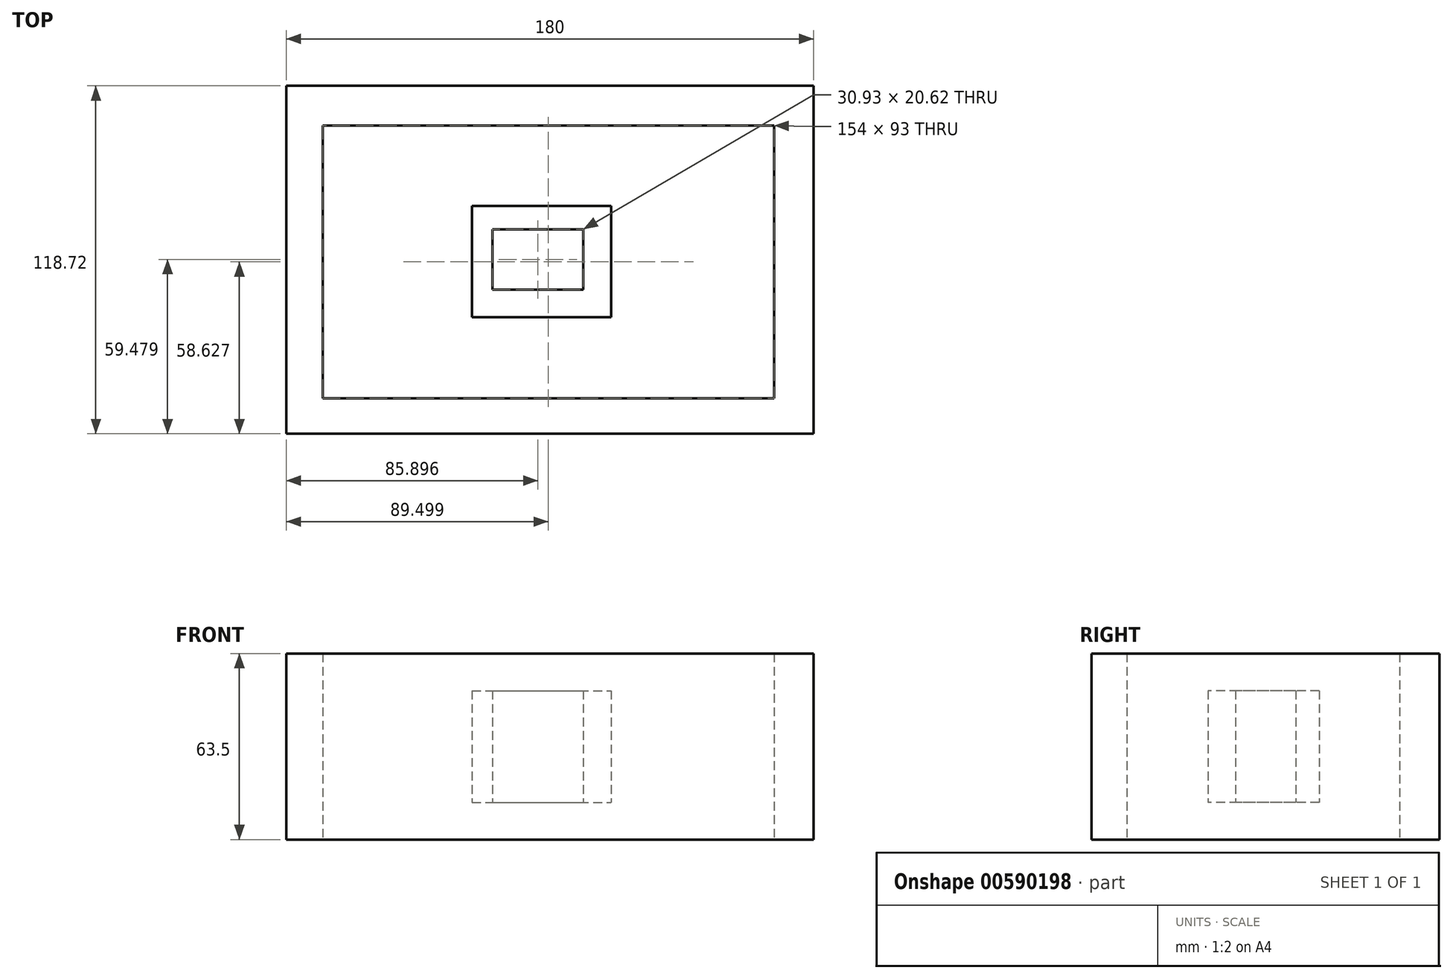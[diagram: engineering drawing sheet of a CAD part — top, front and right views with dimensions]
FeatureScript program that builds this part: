
annotation { "Feature Type Name" : "Feature", "Feature Type Description" : "" }
export const myFeature = defineFeature(function(context is Context, id is Id, definition is map)
    precondition{}
    {
        {
            var Q0;
            Q0=qCreatedBy(makeId("Top.planeOp"),FACE);
            var sketch = newSketch(context, id + "F0", { "sketchPlane" : qUnion([Q0])});
            skLineSegment(sketch, "E0.bottom", {"start": v(-86, 59.95) * mm, "end": v(94, 59.95) * mm});
            skLineSegment(sketch, "E0.top", {"start": v(-86, -58.77) * mm, "end": v(94, -58.77) * mm});
            skLineSegment(sketch, "E0.left", {"start": v(-86, 59.95) * mm, "end": v(-86, -58.77) * mm});
            skLineSegment(sketch, "E0.right", {"start": v(94, 59.95) * mm, "end": v(94, -58.77) * mm});
            skLineSegment(sketch, "E1.bottom", {"start": v(-22.6, 18.99) * mm, "end": v(24.97, 18.99) * mm});
            skLineSegment(sketch, "E1.top", {"start": v(-22.6, -18.99) * mm, "end": v(24.97, -18.99) * mm});
            skLineSegment(sketch, "E1.left", {"start": v(-22.6, 18.99) * mm, "end": v(-22.6, -18.99) * mm});
            skLineSegment(sketch, "E1.right", {"start": v(24.97, 18.99) * mm, "end": v(24.97, -18.99) * mm});
            skLineSegment(sketch, "E2.bottom", {"start": v(-73.5, 46.36) * mm, "end": v(80.5, 46.36) * mm});
            skLineSegment(sketch, "E2.top", {"start": v(-73.5, -46.64) * mm, "end": v(80.5, -46.64) * mm});
            skLineSegment(sketch, "E2.left", {"start": v(-73.5, 46.36) * mm, "end": v(-73.5, -46.64) * mm});
            skLineSegment(sketch, "E2.right", {"start": v(80.5, 46.36) * mm, "end": v(80.5, -46.64) * mm});
            skLineSegment(sketch, "E3.bottom", {"start": v(-15.57, 11.02) * mm, "end": v(15.36, 11.02) * mm});
            skLineSegment(sketch, "E3.top", {"start": v(-15.57, -9.6) * mm, "end": v(15.36, -9.6) * mm});
            skLineSegment(sketch, "E3.left", {"start": v(-15.57, 11.02) * mm, "end": v(-15.57, -9.6) * mm});
            skLineSegment(sketch, "E3.right", {"start": v(15.36, 11.02) * mm, "end": v(15.36, -9.6) * mm});
            skSolve(sketch);
        }
        {
            var Q0;
            Q0=makeQuery(id+"F0.imprint","IMPRINT",FACE,{"disambiguationData":[TD([[makeQuery(id+"F0.imprint","IMPRINT",EDGE,{"derivedFrom":sQuery(id+"F0.wireOp",EDGE,"E0.bottom")}),-1.0]])]});
            extrude(context, id + "F1", {"entities" : qUnion([Q0]), "endBound" : BoundingType.SYMMETRIC, "depth" : 63.5 * mm, "offsetDistance" : 25 * mm});
        }
        {
            var Q0;
            Q0=makeQuery(id+"F0.imprint","IMPRINT",FACE,{"disambiguationData":[TD([[makeQuery(id+"F0.imprint","IMPRINT",EDGE,{"derivedFrom":sQuery(id+"F0.wireOp",EDGE,"E1.bottom")}),-1.0]])]});
            extrude(context, id + "F2", {"entities" : qUnion([Q0]), "endBound" : BoundingType.SYMMETRIC, "depth" : 38.1 * mm, "offsetDistance" : 30.48 * mm});
        }
    });
